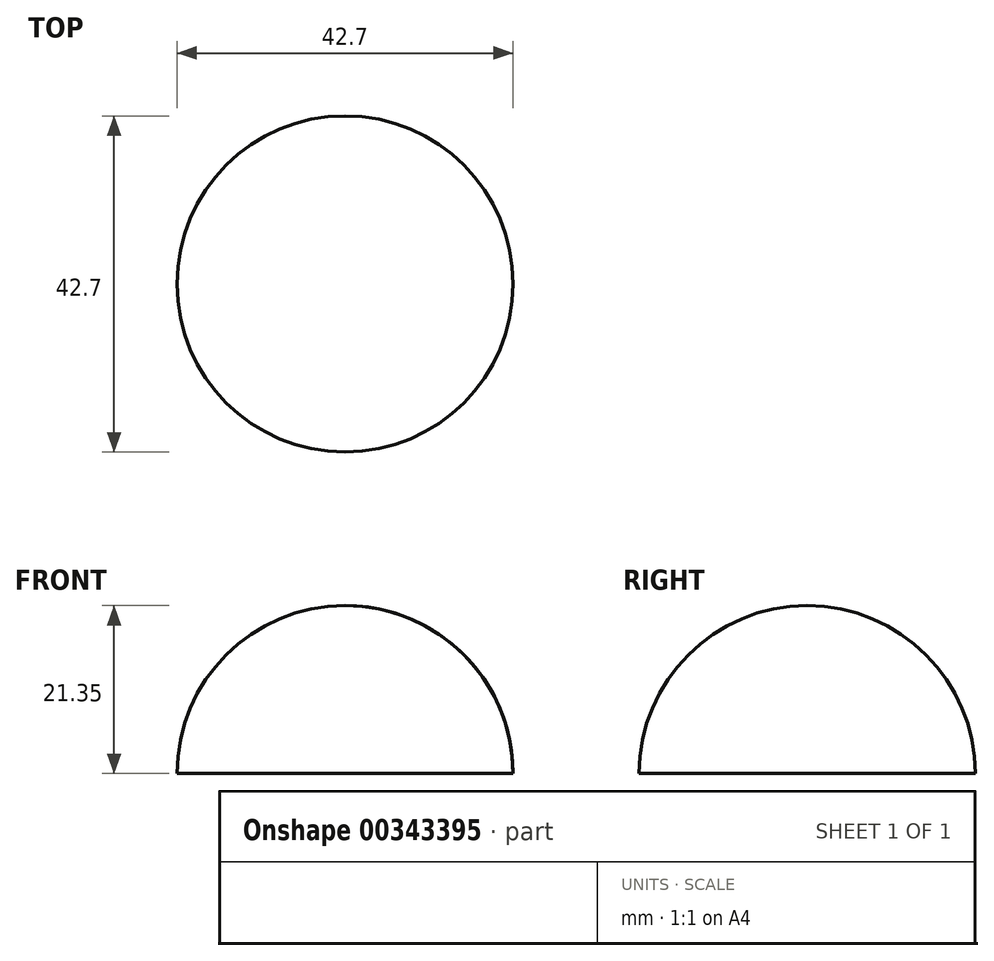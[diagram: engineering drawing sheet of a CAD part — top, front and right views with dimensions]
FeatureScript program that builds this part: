
annotation { "Feature Type Name" : "Feature", "Feature Type Description" : "" }
export const myFeature = defineFeature(function(context is Context, id is Id, definition is map)
    precondition{}
    {
        {
            var Q0;
            Q0=qCreatedBy(makeId("Front.planeOp"),FACE);
            var sketch = newSketch(context, id + "F0", { "sketchPlane" : qUnion([Q0])});
            skArc(sketch, "E0", {"start": v(0, 21.35) * mm, "mid": v(15.1, 15.1) * mm, "end": v(21.35, 0) * mm});
            skLineSegment(sketch, "E1", {"start": v(0, 21.35) * mm, "end": v(0, 0) * mm});
            skLineSegment(sketch, "E2", {"start": v(21.35, 0) * mm, "end": v(0, 0) * mm});
            skSolve(sketch);
        }
        {
            var Q0;
            Q0 = qSketchRegion(id + "F0", true);
            var Q1;
            Q1=sQuery(id+"F0.wireOp",EDGE,"E1");
            revolve(context, id + "F1", {"entities" : qUnion([Q0]), "axis" : qUnion([Q1]), "revolveType" : RevolveType.FULL});
        }
    });
